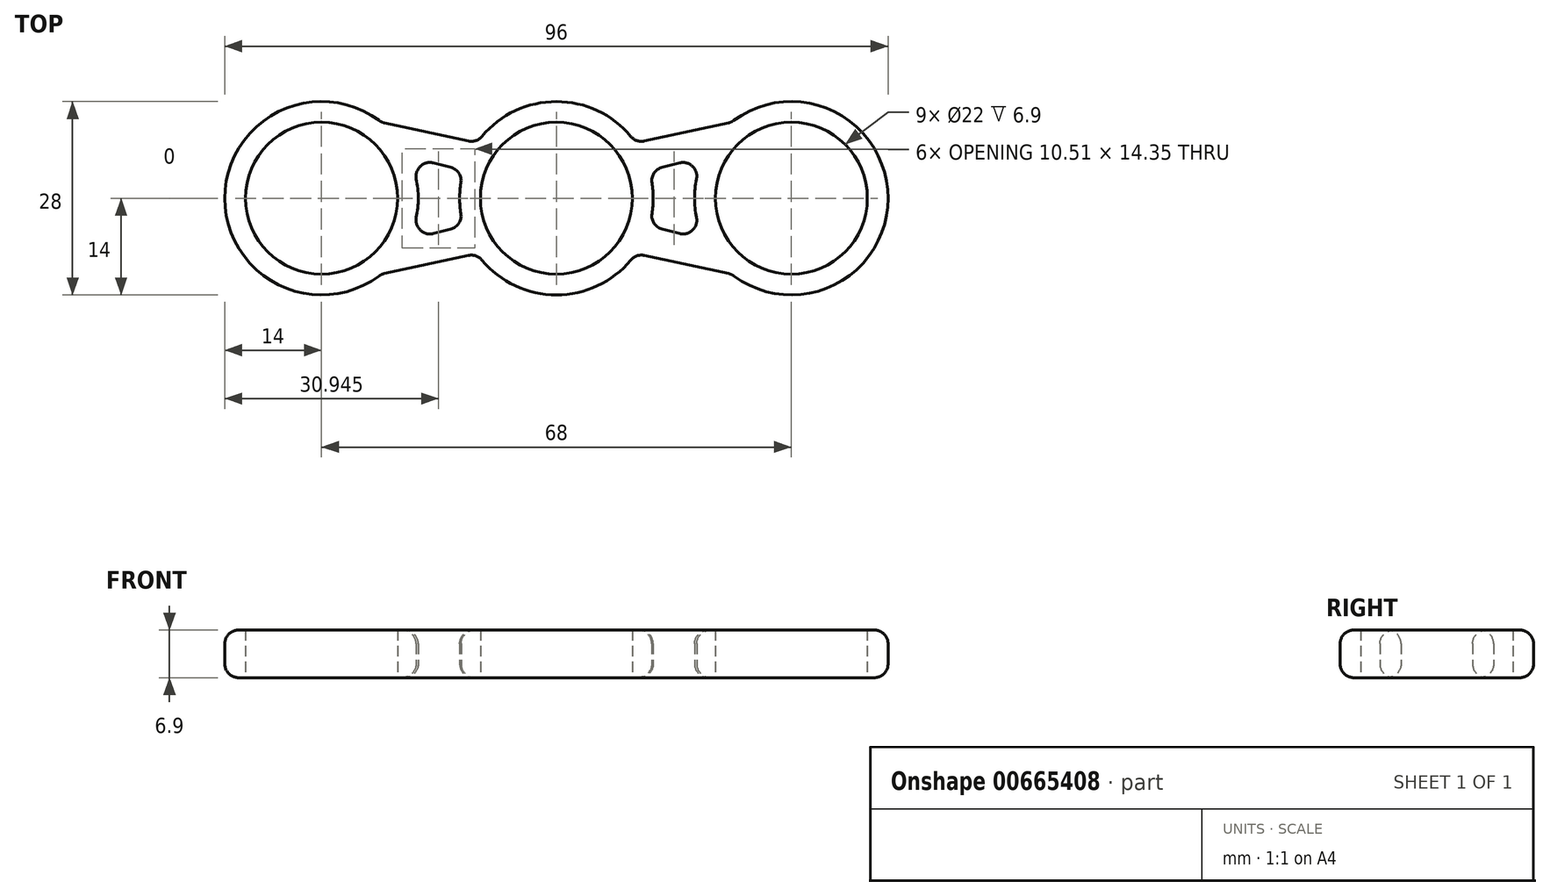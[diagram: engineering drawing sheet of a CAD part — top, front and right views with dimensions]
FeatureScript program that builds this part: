
annotation { "Feature Type Name" : "Feature", "Feature Type Description" : "" }
export const myFeature = defineFeature(function(context is Context, id is Id, definition is map)
    precondition{}
    {
        {
            var Q0;
            Q0=qCreatedBy(makeId("Top.planeOp"),FACE);
            var sketch = newSketch(context, id + "F0", { "sketchPlane" : qUnion([Q0])});
            skLineSegment(sketch, "E0.bottom", {"start": v(48, -16) * mm, "end": v(-48, -16) * mm});
            skLineSegment(sketch, "E0.top", {"start": v(48, 16) * mm, "end": v(-48, 16) * mm});
            skLineSegment(sketch, "E0.left", {"start": v(48, -16) * mm, "end": v(48, 16) * mm});
            skLineSegment(sketch, "E0.right", {"start": v(-48, -16) * mm, "end": v(-48, 16) * mm});
            skPoint(sketch, "E0.middle", {"position": v(0, 0) * mm});
            skLineSegment(sketch, "E1", {"start": v(0, 0) * mm, "end": v(-34, 0) * mm, "construction": true});
            skLineSegment(sketch, "E2", {"start": v(0, 0) * mm, "end": v(34, 0) * mm, "construction": true});
            skCircle(sketch, "E3", {"center": v(-34, 0) * mm, "radius": 11 * mm});
            skCircle(sketch, "E4", {"center": v(0, 0) * mm, "radius": 11 * mm});
            skCircle(sketch, "E5", {"center": v(34, 0) * mm, "radius": 11 * mm});
            skCircle(sketch, "E6", {"center": v(-34, 0) * mm, "radius": 14 * mm});
            skCircle(sketch, "E7", {"center": v(34, 0) * mm, "radius": 14 * mm});
            skCircle(sketch, "E8", {"center": v(0, 0) * mm, "radius": 14 * mm});
            skLineSegment(sketch, "E9.bottom", {"start": v(16, -16) * mm, "end": v(-16, -16) * mm, "construction": true});
            skLineSegment(sketch, "E9.top", {"start": v(16, 16) * mm, "end": v(-16, 16) * mm, "construction": true});
            skLineSegment(sketch, "E9.left", {"start": v(16, -16) * mm, "end": v(16, 16) * mm, "construction": true});
            skLineSegment(sketch, "E9.right", {"start": v(-16, -16) * mm, "end": v(-16, 16) * mm, "construction": true});
            skLineSegment(sketch, "E10.bottom", {"start": v(25.34, -11) * mm, "end": v(-25.34, -11) * mm, "construction": true});
            skLineSegment(sketch, "E10.top", {"start": v(25.34, 11) * mm, "end": v(-25.34, 11) * mm, "construction": true});
            skLineSegment(sketch, "E10.left", {"start": v(25.34, -11) * mm, "end": v(25.34, 11) * mm, "construction": true});
            skLineSegment(sketch, "E10.right", {"start": v(-25.34, -11) * mm, "end": v(-25.34, 11) * mm, "construction": true});
            skLineSegment(sketch, "E11.bottom", {"start": v(13.42, -4) * mm, "end": v(-13.42, -4) * mm, "construction": true});
            skLineSegment(sketch, "E11.top", {"start": v(13.42, 4) * mm, "end": v(-13.42, 4) * mm, "construction": true});
            skLineSegment(sketch, "E11.left", {"start": v(13.42, -4) * mm, "end": v(13.42, 4) * mm, "construction": true});
            skLineSegment(sketch, "E11.right", {"start": v(-13.42, -4) * mm, "end": v(-13.42, 4) * mm, "construction": true});
            skLineSegment(sketch, "E12.bottom", {"start": v(11.48, -8.01) * mm, "end": v(-11.48, -8.01) * mm, "construction": true});
            skLineSegment(sketch, "E12.top", {"start": v(11.48, 8.01) * mm, "end": v(-11.48, 8.01) * mm, "construction": true});
            skLineSegment(sketch, "E12.left", {"start": v(11.48, -8.01) * mm, "end": v(11.48, 8.01) * mm, "construction": true});
            skLineSegment(sketch, "E12.right", {"start": v(-11.48, -8.01) * mm, "end": v(-11.48, 8.01) * mm, "construction": true});
            skLineSegment(sketch, "E13.bottom", {"start": v(21.35, -6) * mm, "end": v(-21.35, -6) * mm, "construction": true});
            skLineSegment(sketch, "E13.top", {"start": v(21.35, 6) * mm, "end": v(-21.35, 6) * mm, "construction": true});
            skLineSegment(sketch, "E13.left", {"start": v(21.35, -6) * mm, "end": v(21.35, 6) * mm, "construction": true});
            skLineSegment(sketch, "E13.right", {"start": v(-21.35, -6) * mm, "end": v(-21.35, 6) * mm, "construction": true});
            skLineSegment(sketch, "E14", {"start": v(-25.34, 11) * mm, "end": v(-11.48, 8.01) * mm});
            skLineSegment(sketch, "E15", {"start": v(-13.42, 4) * mm, "end": v(-21.35, 6) * mm});
            skLineSegment(sketch, "E16", {"start": v(-21.35, -6) * mm, "end": v(-13.42, -4) * mm});
            skLineSegment(sketch, "E17", {"start": v(-25.34, -11) * mm, "end": v(-11.48, -8.01) * mm});
            skLineSegment(sketch, "E18", {"start": v(11.48, 8.01) * mm, "end": v(25.34, 11) * mm});
            skLineSegment(sketch, "E19", {"start": v(21.35, 6) * mm, "end": v(13.42, 4) * mm});
            skLineSegment(sketch, "E20", {"start": v(13.42, -4) * mm, "end": v(21.35, -6) * mm});
            skLineSegment(sketch, "E21", {"start": v(25.34, -11) * mm, "end": v(11.48, -8.01) * mm});
            skSolve(sketch);
        }
        {
            var Q0;
            Q0=makeQuery(id+"F0.imprint","IMPRINT",FACE,{"disambiguationData":[TD([[makeQuery(id+"F0.imprint","IMPRINT",EDGE,{"derivedFrom":sQuery(id+"F0.wireOp",EDGE,"E3")}),-1.0]])]});
            var Q1;
            {var subQ0=sQuery(id+"F0.wireOp",EDGE,"E14");Q1=makeQuery(id+"F0.imprint","IMPRINT",FACE,{"disambiguationData":[TD([[makeQuery(id+"F0.imprint","IMPRINT",EDGE,{"derivedFrom":subQ0}),-1.0]])]});}
            var Q2;
            {var subQ0=sQuery(id+"F0.wireOp",EDGE,"E16");Q2=makeQuery(id+"F0.imprint","IMPRINT",FACE,{"disambiguationData":[TD([[makeQuery(id+"F0.imprint","IMPRINT",EDGE,{"derivedFrom":subQ0}),-1.0]])]});}
            var Q3;
            Q3=makeQuery(id+"F0.imprint","IMPRINT",FACE,{"disambiguationData":[TD([[makeQuery(id+"F0.imprint","IMPRINT",EDGE,{"derivedFrom":sQuery(id+"F0.wireOp",EDGE,"E4")}),-1.0]])]});
            var Q4;
            {var subQ0=sQuery(id+"F0.wireOp",EDGE,"E18");Q4=makeQuery(id+"F0.imprint","IMPRINT",FACE,{"disambiguationData":[TD([[makeQuery(id+"F0.imprint","IMPRINT",EDGE,{"derivedFrom":subQ0}),-1.0]])]});}
            var Q5;
            {var subQ0=sQuery(id+"F0.wireOp",EDGE,"E20");Q5=makeQuery(id+"F0.imprint","IMPRINT",FACE,{"disambiguationData":[TD([[makeQuery(id+"F0.imprint","IMPRINT",EDGE,{"derivedFrom":subQ0}),-1.0]])]});}
            var Q6;
            Q6=makeQuery(id+"F0.imprint","IMPRINT",FACE,{"disambiguationData":[TD([[makeQuery(id+"F0.imprint","IMPRINT",EDGE,{"derivedFrom":sQuery(id+"F0.wireOp",EDGE,"E5")}),-1.0]])]});
            extrude(context, id + "F1", {"entities" : qUnion([Q0, Q1, Q2, Q3, Q4, Q5, Q6]), "depth" : 6.9 * mm, "offsetDistance" : 25 * mm});
        }
        {
            var Q0;
            {var subQ0=sQuery(id+"F0.wireOp",EDGE,"E6");Q0=makeQuery(id+"F1.opExtrude","SWEPT_FACE",FACE,{"disambiguationData":[OSD([subQ0]),TDD([makeQuery(id+"F0.imprint","IMPRINT",EDGE,{"disambiguationData":[TD([[makeQuery(id+"F0.imprint","INTERSECT",VERTEX,{"derivedFrom":[subQ0,sQuery(id+"F0.wireOp",EDGE,"E14")]}),-1.0]])],"derivedFrom":subQ0}),makeQuery(id+"F0.imprint","IMPRINT",EDGE,{"disambiguationData":[TD([[makeQuery(id+"F0.imprint","INTERSECT",VERTEX,{"derivedFrom":[subQ0,sQuery(id+"F0.wireOp",EDGE,"E17")]}),1.0]])],"derivedFrom":subQ0})])]});}
            var Q1;
            Q1=makeQuery(id+"F1.opExtrude","SWEPT_FACE",FACE,{"disambiguationData":[OSD([sQuery(id+"F0.wireOp",EDGE,"E14")])]});
            var Q2;
            {var subQ0=sQuery(id+"F0.wireOp",EDGE,"E8");Q2=makeQuery(id+"F1.opExtrude","SWEPT_FACE",FACE,{"disambiguationData":[OSD([subQ0]),TDD([makeQuery(id+"F0.imprint","IMPRINT",EDGE,{"disambiguationData":[TD([[makeQuery(id+"F0.imprint","INTERSECT",VERTEX,{"derivedFrom":[subQ0,sQuery(id+"F0.wireOp",EDGE,"E14")]}),1.0]])],"derivedFrom":subQ0})])]});}
            var Q3;
            Q3=makeQuery(id+"F1.opExtrude","SWEPT_FACE",FACE,{"disambiguationData":[OSD([sQuery(id+"F0.wireOp",EDGE,"E18")])]});
            var Q4;
            {var subQ0=sQuery(id+"F0.wireOp",EDGE,"E7");Q4=makeQuery(id+"F1.opExtrude","SWEPT_FACE",FACE,{"disambiguationData":[OSD([subQ0]),TDD([makeQuery(id+"F0.imprint","IMPRINT",EDGE,{"disambiguationData":[TD([[makeQuery(id+"F0.imprint","INTERSECT",VERTEX,{"derivedFrom":[subQ0,sQuery(id+"F0.wireOp",EDGE,"E18")]}),1.0]])],"derivedFrom":subQ0}),makeQuery(id+"F0.imprint","IMPRINT",EDGE,{"disambiguationData":[TD([[makeQuery(id+"F0.imprint","INTERSECT",VERTEX,{"derivedFrom":[subQ0,sQuery(id+"F0.wireOp",EDGE,"E21")]}),-1.0]])],"derivedFrom":subQ0})])]});}
            var Q5;
            Q5=makeQuery(id+"F1.opExtrude","SWEPT_FACE",FACE,{"disambiguationData":[OSD([sQuery(id+"F0.wireOp",EDGE,"E21")])]});
            var Q6;
            {var subQ0=sQuery(id+"F0.wireOp",EDGE,"E8");Q6=makeQuery(id+"F1.opExtrude","SWEPT_FACE",FACE,{"disambiguationData":[OSD([subQ0]),TDD([makeQuery(id+"F0.imprint","IMPRINT",EDGE,{"disambiguationData":[TD([[makeQuery(id+"F0.imprint","INTERSECT",VERTEX,{"derivedFrom":[subQ0,sQuery(id+"F0.wireOp",EDGE,"E17")]}),-1.0]])],"derivedFrom":subQ0})])]});}
            var Q7;
            Q7=makeQuery(id+"F1.opExtrude","SWEPT_FACE",FACE,{"disambiguationData":[OSD([sQuery(id+"F0.wireOp",EDGE,"E17")])]});
            var Q8;
            Q8=makeQuery(id+"F1.opExtrude","SWEPT_FACE",FACE,{"disambiguationData":[OSD([sQuery(id+"F0.wireOp",EDGE,"E15")])]});
            var Q9;
            Q9=makeQuery(id+"F1.opExtrude","SWEPT_FACE",FACE,{"disambiguationData":[OSD([sQuery(id+"F0.wireOp",EDGE,"E19")])]});
            var Q10;
            {var subQ0=sQuery(id+"F0.wireOp",EDGE,"E6");Q10=makeQuery(id+"F1.opExtrude","SWEPT_FACE",FACE,{"disambiguationData":[OSD([subQ0]),TDD([makeQuery(id+"F0.imprint","IMPRINT",EDGE,{"disambiguationData":[TD([[makeQuery(id+"F0.imprint","INTERSECT",VERTEX,{"derivedFrom":[subQ0,sQuery(id+"F0.wireOp",EDGE,"E15")]}),1.0]])],"derivedFrom":subQ0})])]});}
            var Q11;
            {var subQ0=sQuery(id+"F0.wireOp",EDGE,"E8");Q11=makeQuery(id+"F1.opExtrude","SWEPT_FACE",FACE,{"disambiguationData":[OSD([subQ0]),TDD([makeQuery(id+"F0.imprint","IMPRINT",EDGE,{"disambiguationData":[TD([[makeQuery(id+"F0.imprint","INTERSECT",VERTEX,{"derivedFrom":[subQ0,sQuery(id+"F0.wireOp",EDGE,"E19")]}),1.0]])],"derivedFrom":subQ0})])]});}
            var Q12;
            {var subQ0=sQuery(id+"F0.wireOp",EDGE,"E8");Q12=makeQuery(id+"F1.opExtrude","SWEPT_FACE",FACE,{"disambiguationData":[OSD([subQ0]),TDD([makeQuery(id+"F0.imprint","IMPRINT",EDGE,{"disambiguationData":[TD([[makeQuery(id+"F0.imprint","INTERSECT",VERTEX,{"derivedFrom":[subQ0,sQuery(id+"F0.wireOp",EDGE,"E15")]}),-1.0]])],"derivedFrom":subQ0})])]});}
            var Q13;
            {var subQ0=sQuery(id+"F0.wireOp",EDGE,"E7");Q13=makeQuery(id+"F1.opExtrude","SWEPT_FACE",FACE,{"disambiguationData":[OSD([subQ0]),TDD([makeQuery(id+"F0.imprint","IMPRINT",EDGE,{"disambiguationData":[TD([[makeQuery(id+"F0.imprint","INTERSECT",VERTEX,{"derivedFrom":[subQ0,sQuery(id+"F0.wireOp",EDGE,"E19")]}),-1.0]])],"derivedFrom":subQ0})])]});}
            var Q14;
            Q14=makeQuery(id+"F1.opExtrude","SWEPT_FACE",FACE,{"disambiguationData":[OSD([sQuery(id+"F0.wireOp",EDGE,"E20")])]});
            var Q15;
            Q15=makeQuery(id+"F1.opExtrude","SWEPT_FACE",FACE,{"disambiguationData":[OSD([sQuery(id+"F0.wireOp",EDGE,"E16")])]});
            fillet(context, id + "F2", {"entities" : qUnion([Q0, Q1, Q2, Q3, Q4, Q5, Q6, Q7, Q8, Q9, Q10, Q11, Q12, Q13, Q14, Q15]), "radius" : 2 * mm, "tangentPropagation" : true, "allowEdgeOverflow" : false});
        }
    });
